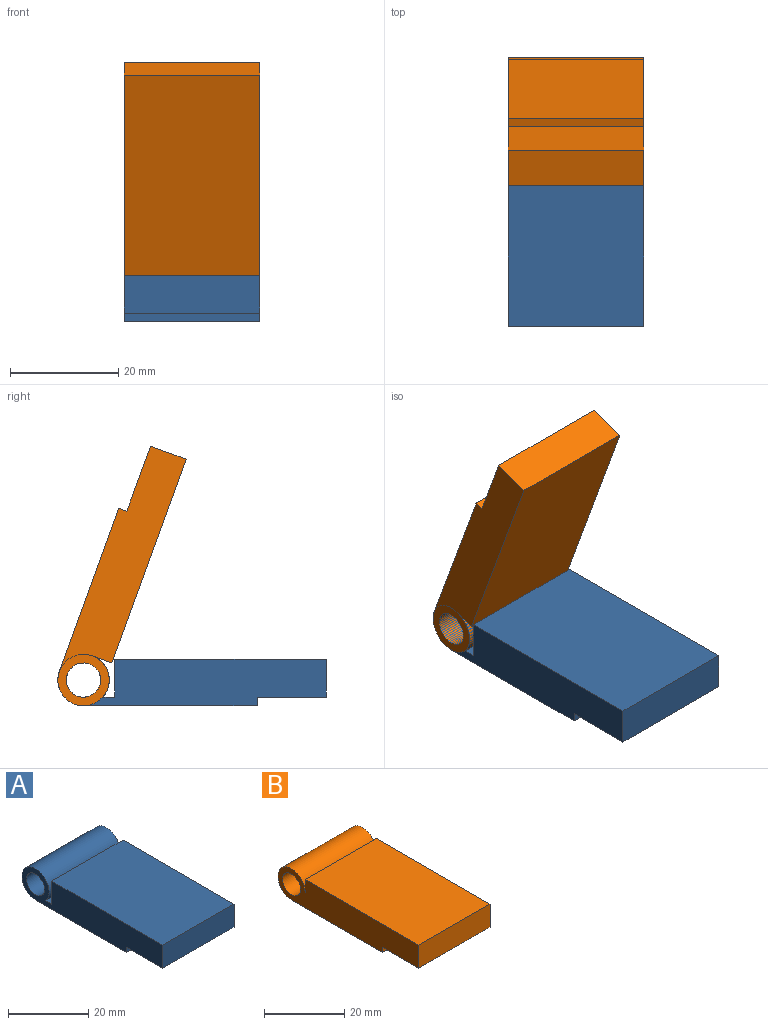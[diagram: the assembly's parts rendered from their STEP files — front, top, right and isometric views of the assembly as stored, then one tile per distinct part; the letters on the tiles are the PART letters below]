
ASSEMBLY  parts=2 mates=1
PART A: 11 faces, bbox 25x49.5x9.5 mm
  f0: plane 25x12.75mm, normal (0,0,-1), area 318.8mm2, adj f1,f7,f9,f10
  f1: plane 25x1.6mm, normal (0,-1,0), area 40mm2, adj f0,f2,f9,f10
  f2: plane 32x25mm, normal (0,0,-1), area 800mm2, adj f1,f3,f9,f10
  f3: cylinder r=4.75mm len=25mm, axis (-1,0,0), area 645.7mm2, adj f2,f4,f9,f10
  f4: plane 25x2.19mm, normal (0,0,1), area 54.9mm2, adj f3,f5,f9,f10
  f5: plane 25x7mm, normal (0,1,0), area 175mm2, adj f4,f6,f9,f10
  f6: plane 39x25mm, normal (0,0,1), area 975mm2, adj f5,f7,f9,f10
  f7: plane 25x7mm, normal (0,-1,0), area 175mm2, adj f0,f6,f9,f10
  f8: cylinder r=3.15mm len=25mm, axis (-1,0,0), area 494.8mm2, adj f9,f10
  f9: plane 49.5x9.5mm, normal (1,0,0), area 360mm2, adj f0,f1,f2,f3,f4,f5,f6,f7
  f10: plane 49.5x9.5mm, normal (-1,0,0), area 360mm2, adj f0,f1,f2,f3,f4,f5,f6,f7
PART B: 10 faces, bbox 25x49.5x9.5 mm
  f0: plane 40x25mm, normal (0,0,1), area 1000mm2, adj f1,f6,f8,f9
  f1: plane 25x7mm, normal (0,-1,0), area 175mm2, adj f0,f2,f8,f9
  f2: plane 25x12.75mm, normal (0,0,-1), area 318.8mm2, adj f1,f3,f8,f9
  f3: plane 25x1.6mm, normal (0,-1,0), area 40mm2, adj f2,f4,f8,f9
  f4: plane 32x25mm, normal (0,0,-1), area 800mm2, adj f3,f5,f8,f9
  f5: cylinder r=4.75mm len=25mm, axis (-1,0,0), area 559.6mm2, adj f4,f6,f8,f9
  f6: plane 25x3.85mm, normal (0,1,0), area 96.2mm2, adj f0,f5,f8,f9
  f7: cylinder r=3.15mm len=25mm, axis (-1,0,0), area 494.8mm2, adj f8,f9
  f8: plane 49.5x9.5mm, normal (1,0,0), area 368.2mm2, adj f0,f1,f2,f3,f4,f5,f6,f7
  f9: plane 49.5x9.5mm, normal (-1,0,0), area 368.2mm2, adj f0,f1,f2,f3,f4,f5,f6,f7
PLACE A t=(-15.82,12.75,-11.15)mm
PLACE B rot(axis=(0,-0.82,0.57),180deg) t=(9.18,15.71,-6.92)mm
MATE revolute B.f5 <-> A.f3  axis (1,0,0) through (9.18,12.75,-8)mm
